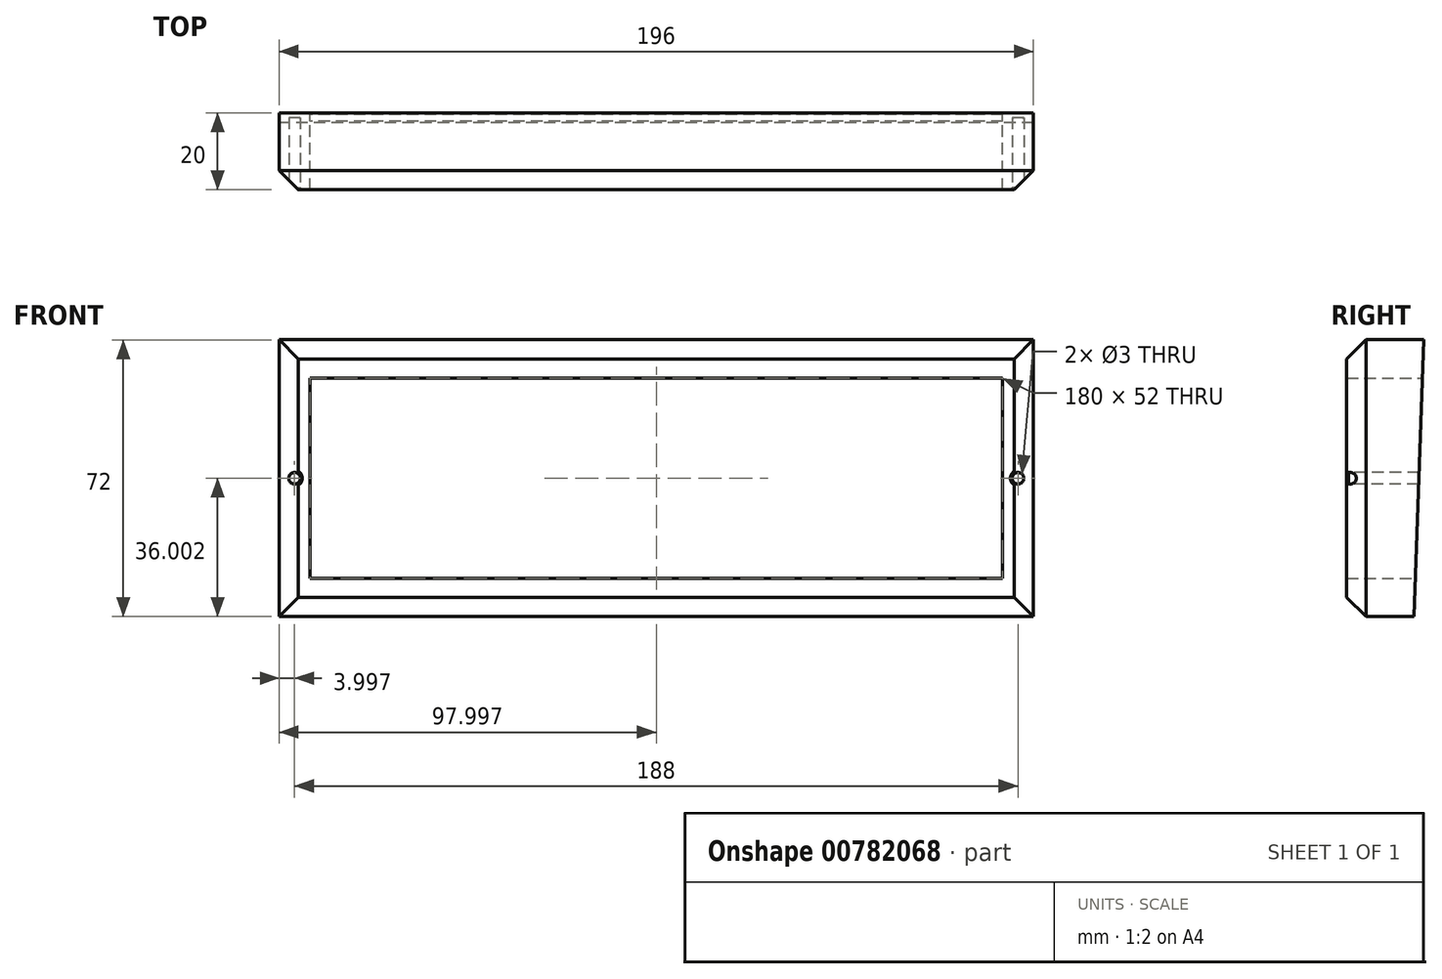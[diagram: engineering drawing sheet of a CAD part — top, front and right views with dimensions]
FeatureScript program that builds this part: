
annotation { "Feature Type Name" : "Feature", "Feature Type Description" : "" }
export const myFeature = defineFeature(function(context is Context, id is Id, definition is map)
    precondition{}
    {
        {
            var Q0;
            Q0=qCreatedBy(makeId("Front.planeOp"),FACE);
            var sketch = newSketch(context, id + "F0", { "sketchPlane" : qUnion([Q0])});
            skLineSegment(sketch, "E0.bottom", {"start": v(-88.57, 32.98) * mm, "end": v(91.43, 32.98) * mm});
            skLineSegment(sketch, "E0.top", {"start": v(-88.57, -19.02) * mm, "end": v(91.43, -19.02) * mm});
            skLineSegment(sketch, "E0.left", {"start": v(-88.57, 32.98) * mm, "end": v(-88.57, -19.02) * mm});
            skLineSegment(sketch, "E0.right", {"start": v(91.43, 32.98) * mm, "end": v(91.43, -19.02) * mm});
            skLineSegment(sketch, "E1.bottom", {"start": v(-96.57, 42.98) * mm, "end": v(99.43, 42.98) * mm});
            skLineSegment(sketch, "E1.top", {"start": v(-96.57, -29.02) * mm, "end": v(99.43, -29.02) * mm});
            skLineSegment(sketch, "E1.left", {"start": v(-96.57, 42.98) * mm, "end": v(-96.57, -29.02) * mm});
            skLineSegment(sketch, "E1.right", {"start": v(99.43, 42.98) * mm, "end": v(99.43, -29.02) * mm});
            skSolve(sketch);
        }
        {
            var Q0;
            Q0=makeQuery(id+"F0.imprint","IMPRINT",FACE,{"disambiguationData":[TD([[makeQuery(id+"F0.imprint","IMPRINT",EDGE,{"derivedFrom":sQuery(id+"F0.wireOp",EDGE,"E0.bottom")}),1.0]])]});
            extrude(context, id + "F1", {"entities" : qUnion([Q0]), "depth" : 20 * mm, "offsetDistance" : 25 * mm});
        }
        {
            var Q0;
            Q0=makeQuery(id+"F1.opExtrude","SWEPT_FACE",FACE,{"disambiguationData":[OSD([sQuery(id+"F0.wireOp",EDGE,"E1.left")])]});
            var sketch = newSketch(context, id + "F2", { "sketchPlane" : qUnion([Q0])});
            skLineSegment(sketch, "E2", {"start": v(0, 42.98) * mm, "end": v(2.5, -29.02) * mm});
            skSolve(sketch);
        }
        {
            var Q0;
            {var subQ0=sQuery(id+"F2.wireOp",EDGE,"E2");Q0=makeQuery(id+"F2.imprint","IMPRINT",FACE,{"disambiguationData":[TD([[makeQuery(id+"F2.imprint","IMPRINT",EDGE,{"derivedFrom":subQ0}),-1.0]])]});}
            extrude(context, id + "F3", {"entities" : qUnion([Q0]), "operationType" : NewBodyOperationType.REMOVE, "oppositeDirection" : true, "depth" : 228.8 * mm, "offsetDistance" : 25 * mm});
        }
        {
            var Q0;
            Q0=makeQuery(id+"F1.opExtrude","CAP_FACE",FACE,{"disambiguationData":[OSD([sQuery(id+"F0.wireOp",EDGE,"E0.bottom"),sQuery(id+"F0.wireOp",EDGE,"E0.top"),sQuery(id+"F0.wireOp",EDGE,"E0.left"),sQuery(id+"F0.wireOp",EDGE,"E0.right"),sQuery(id+"F0.wireOp",EDGE,"E1.bottom"),sQuery(id+"F0.wireOp",EDGE,"E1.top"),sQuery(id+"F0.wireOp",EDGE,"E1.left"),sQuery(id+"F0.wireOp",EDGE,"E1.right")])],"isStart":false});
            var sketch = newSketch(context, id + "F4", { "sketchPlane" : qUnion([Q0])});
            skPoint(sketch, "E3", {"position": v(95.43, 6.98) * mm});
            skPoint(sketch, "E3.positionSnap0", {"position": v(99.43, 6.98) * mm});
            skPoint(sketch, "E4", {"position": v(-92.57, 6.98) * mm});
            skPoint(sketch, "E4.positionSnap0", {"position": v(91.43, 6.98) * mm});
            skSolve(sketch);
        }
        {
            var Q0;
            Q0=sQuery(id+"F4.wireOp",VERTEX,"E4");
            var Q1;
            Q1=sQuery(id+"F4.wireOp",VERTEX,"E3");
            var Q2;
            Q2=makeQuery(id+"F1.opExtrude","SWEPT_BODY",BODY,{"disambiguationData":[OSD([sQuery(id+"F0.wireOp",EDGE,"E0.bottom"),sQuery(id+"F0.wireOp",EDGE,"E0.top"),sQuery(id+"F0.wireOp",EDGE,"E0.left"),sQuery(id+"F0.wireOp",EDGE,"E0.right"),sQuery(id+"F0.wireOp",EDGE,"E1.bottom"),sQuery(id+"F0.wireOp",EDGE,"E1.top"),sQuery(id+"F0.wireOp",EDGE,"E1.left"),sQuery(id+"F0.wireOp",EDGE,"E1.right")])]});
            hole(context, id + "F5", {"style" : HoleStyle.C_SINK, "endStyle" : HoleEndStyle.BLIND, "holeDiameter" : 3 * mm, "cSinkDiameter" : 4 * mm, "cSinkAngle" : 90 * degree, "majorDiameter" : 5 * mm, "holeDepth" : 25 * mm, "isTappedThrough" : true, "tappedDepth" : 12 * mm, "tapClearance" : 3, "locations" : qUnion([Q0, Q1]), "scope" : qUnion([Q2])});
        }
        {
            var Q0;
            Q0=makeQuery(id+"F1.opExtrude","CAP_EDGE",EDGE,{"disambiguationData":[OSD([sQuery(id+"F0.wireOp",EDGE,"E1.bottom")])],"isStart":false});
            var Q1;
            Q1=makeQuery(id+"F1.opExtrude","CAP_EDGE",EDGE,{"disambiguationData":[OSD([sQuery(id+"F0.wireOp",EDGE,"E1.left")])],"isStart":false});
            var Q2;
            Q2=makeQuery(id+"F1.opExtrude","CAP_EDGE",EDGE,{"disambiguationData":[OSD([sQuery(id+"F0.wireOp",EDGE,"E1.top")])],"isStart":false});
            var Q3;
            Q3=makeQuery(id+"F1.opExtrude","CAP_EDGE",EDGE,{"disambiguationData":[OSD([sQuery(id+"F0.wireOp",EDGE,"E1.right")])],"isStart":false});
            chamfer(context, id + "F6", {"entities" : qUnion([Q0, Q1, Q2, Q3]), "width" : 5 * mm, "tangentPropagation" : true});
        }
    });
